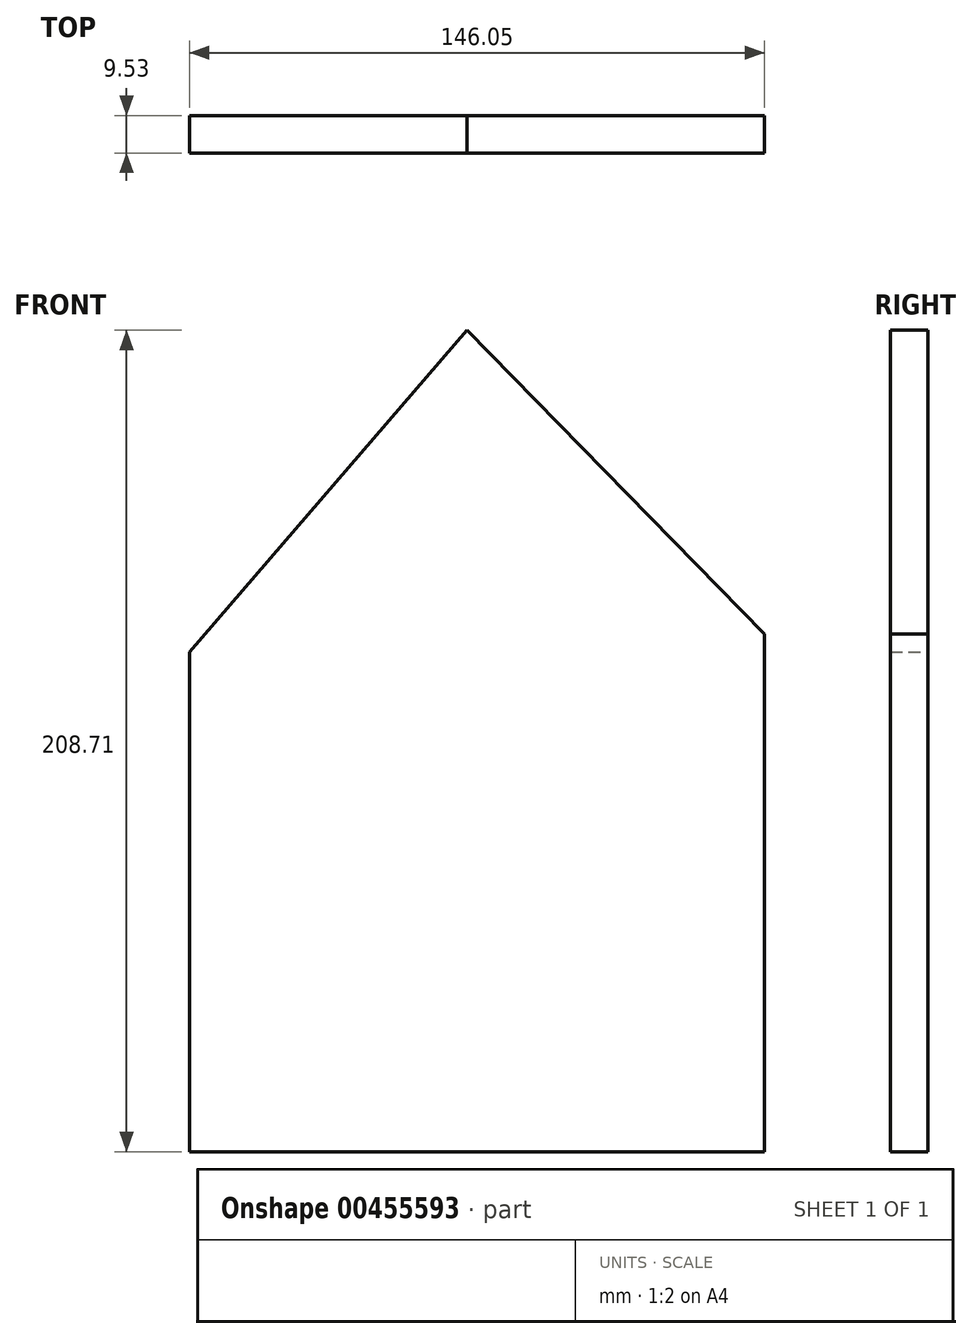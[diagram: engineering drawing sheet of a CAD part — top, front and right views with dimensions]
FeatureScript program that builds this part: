
annotation { "Feature Type Name" : "Feature", "Feature Type Description" : "" }
export const myFeature = defineFeature(function(context is Context, id is Id, definition is map)
    precondition{}
    {
        {
            var Q0;
            Q0=qCreatedBy(makeId("Front.planeOp"),FACE);
            var sketch = newSketch(context, id + "F0", { "sketchPlane" : qUnion([Q0])});
            skLineSegment(sketch, "E0", {"start": v(0, 0) * mm, "end": v(146.05, 0) * mm});
            skLineSegment(sketch, "E1", {"start": v(146.05, 0) * mm, "end": v(146.05, 131.57) * mm});
            skLineSegment(sketch, "E2", {"start": v(146.05, 131.57) * mm, "end": v(70.54, 208.71) * mm});
            skLineSegment(sketch, "E3", {"start": v(70.54, 208.71) * mm, "end": v(0, 127) * mm});
            skLineSegment(sketch, "E4", {"start": v(0, 127) * mm, "end": v(0, 0) * mm});
            skSolve(sketch);
        }
        {
            var Q0;
            Q0 = qSketchRegion(id + "F0", true);
            extrude(context, id + "F1", {"entities" : qUnion([Q0]), "depth" : 9.52 * mm});
        }
    });
